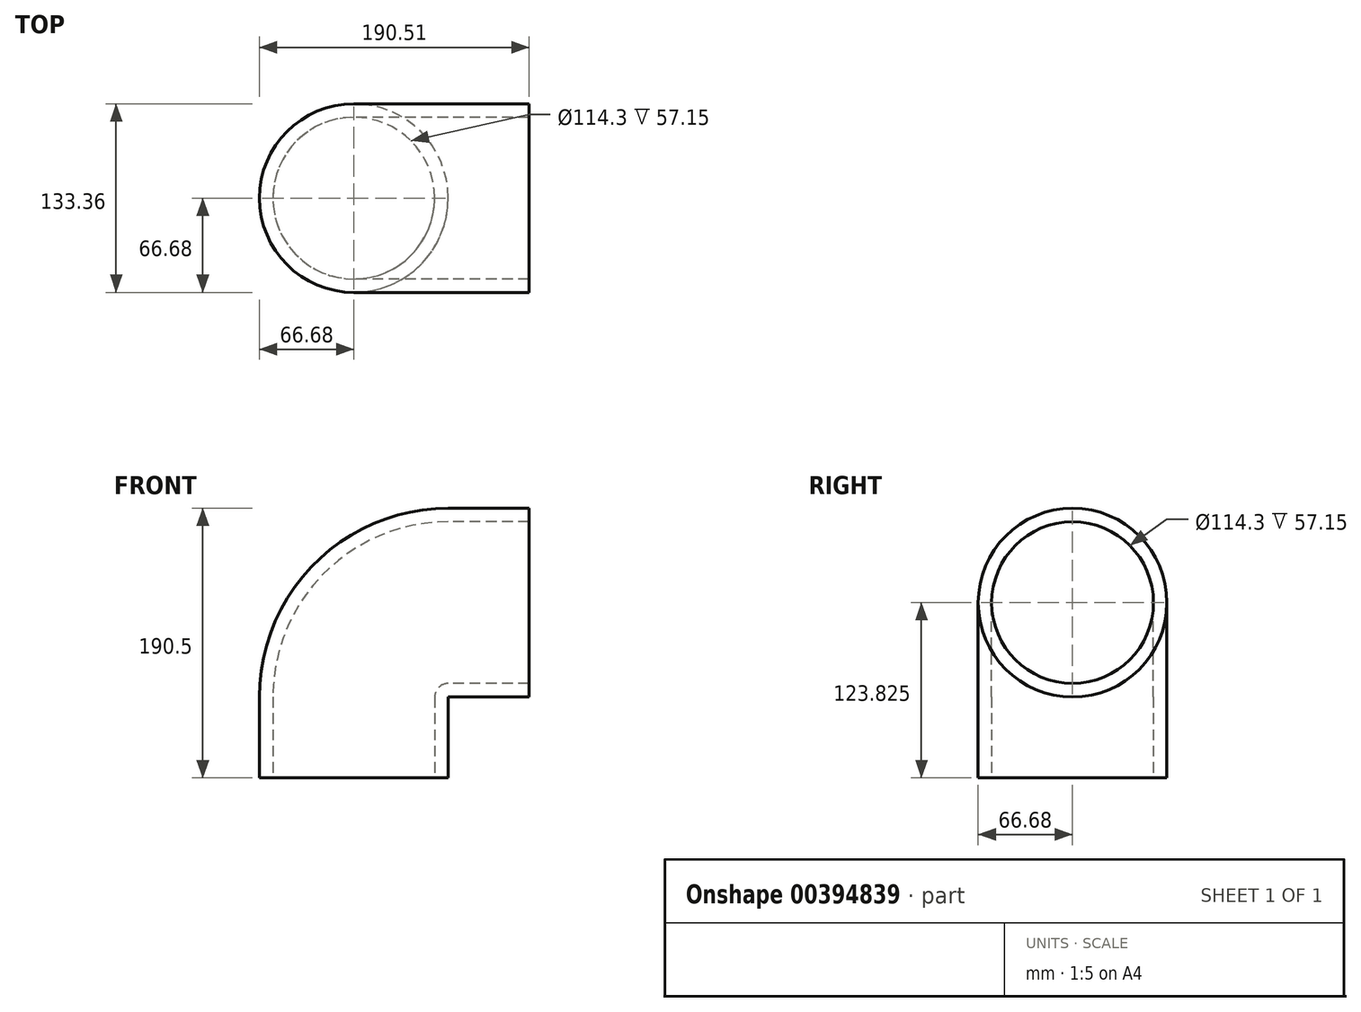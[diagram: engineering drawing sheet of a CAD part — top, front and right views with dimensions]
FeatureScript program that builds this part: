
annotation { "Feature Type Name" : "Feature", "Feature Type Description" : "" }
export const myFeature = defineFeature(function(context is Context, id is Id, definition is map)
    precondition{}
    {
        {
            var Q0;
            Q0=qCreatedBy(makeId("Top.planeOp"),FACE);
            var sketch = newSketch(context, id + "F0", { "sketchPlane" : qUnion([Q0])});
            skCircle(sketch, "E0", {"center": v(0, 0) * mm, "radius": 57.15 * mm});
            skCircle(sketch, "E1", {"center": v(0, 0) * mm, "radius": 66.68 * mm});
            skSolve(sketch);
        }
        {
            var Q0;
            Q0=makeQuery(id+"F0.imprint","IMPRINT",FACE,{"disambiguationData":[TD([[makeQuery(id+"F0.imprint","IMPRINT",EDGE,{"derivedFrom":sQuery(id+"F0.wireOp",EDGE,"E0")}),-1.0]])]});
            extrude(context, id + "F1", {"entities" : qUnion([Q0]), "depth" : 57.15 * mm});
        }
        {
            var Q0;
            Q0=makeQuery(id+"F1.opExtrude","CAP_FACE",FACE,{"disambiguationData":[OSD([sQuery(id+"F0.wireOp",EDGE,"E0"),sQuery(id+"F0.wireOp",EDGE,"E1")])],"isStart":false});
            var sketch = newSketch(context, id + "F2", { "sketchPlane" : qUnion([Q0])});
            skLineSegment(sketch, "E2", {"start": v(66.68, 0) * mm, "end": v(66.68, 47.5) * mm, "construction": true});
            skSolve(sketch);
        }
        {
            var Q0;
            Q0=makeQuery(id+"F2.imprint","IMPRINT",FACE,{"disambiguationData":[TD([[makeQuery(id+"F2.imprint","IMPRINT",EDGE,{"derivedFrom":makeQuery(id+"F1.opExtrude","CAP_EDGE",EDGE,{"disambiguationData":[OSD([sQuery(id+"F0.wireOp",EDGE,"E0")])],"isStart":false})}),-1.0]])]});
            var Q1;
            Q1=sQuery(id+"F2.wireOp",EDGE,"E2");
            revolve(context, id + "F3", {"operationType" : NewBodyOperationType.ADD, "entities" : qUnion([Q0]), "axis" : qUnion([Q1]), "revolveType" : RevolveType.ONE_DIRECTION, "angle" : 90 * degree});
        }
        {
            var Q0;
            Q0=makeQuery(id+"F3.opRevolve","CAP_FACE",FACE,{"disambiguationData":[OSD([sQuery(id+"F0.wireOp",EDGE,"E0"),sQuery(id+"F0.wireOp",EDGE,"E1")])],"isStart":false});
            extrude(context, id + "F4", {"entities" : qUnion([Q0]), "operationType" : NewBodyOperationType.ADD, "depth" : 57.15 * mm});
        }
    });
